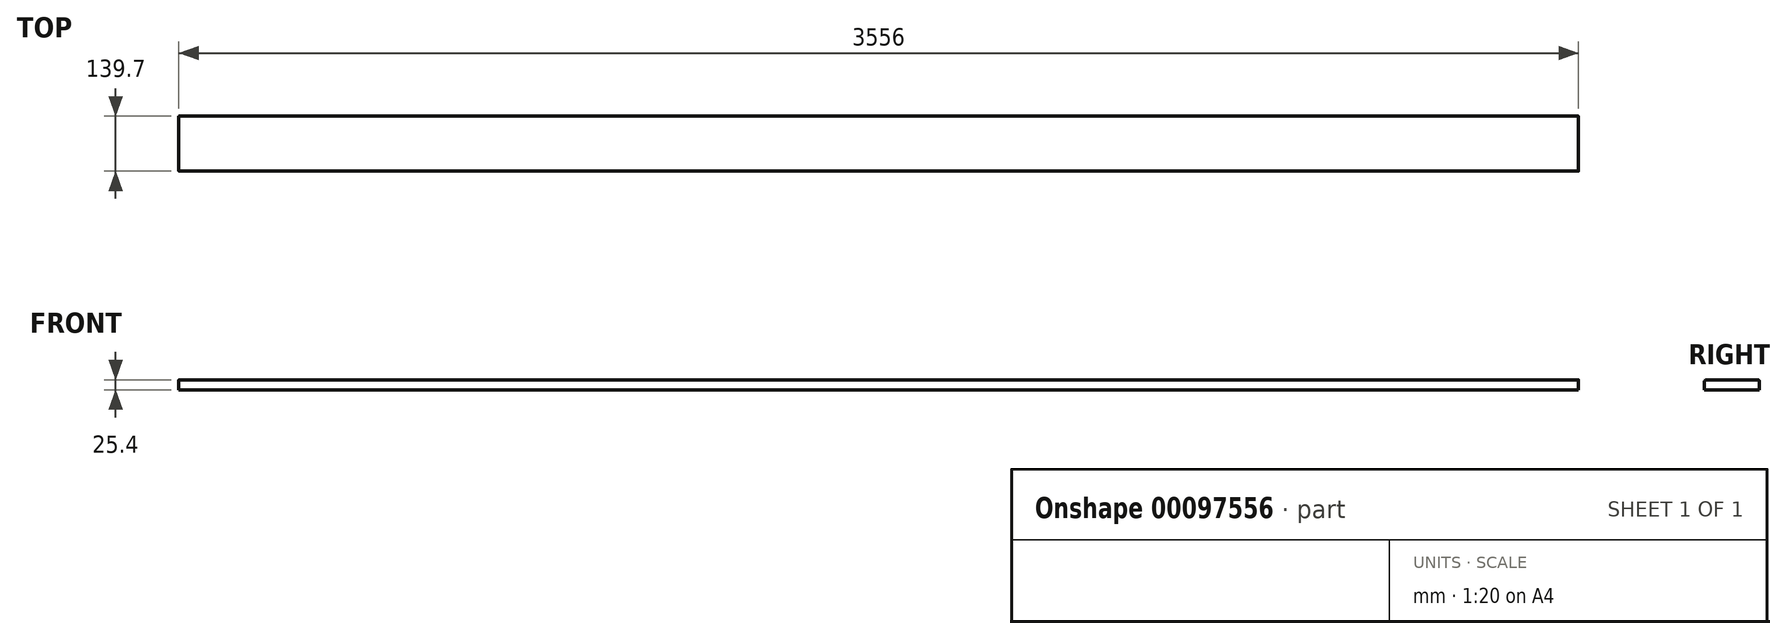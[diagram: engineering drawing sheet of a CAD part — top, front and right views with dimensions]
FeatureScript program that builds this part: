
annotation { "Feature Type Name" : "Feature", "Feature Type Description" : "" }
export const myFeature = defineFeature(function(context is Context, id is Id, definition is map)
    precondition{}
    {
        {
            var Q0;
            Q0=qCreatedBy(makeId("Top.planeOp"),FACE);
            var sketch = newSketch(context, id + "F0", { "sketchPlane" : qUnion([Q0])});
            skLineSegment(sketch, "E0.bottom", {"start": v(1778, 69.85) * mm, "end": v(-1778, 69.85) * mm});
            skLineSegment(sketch, "E0.top", {"start": v(1778, -69.85) * mm, "end": v(-1778, -69.85) * mm});
            skLineSegment(sketch, "E0.left", {"start": v(1778, 69.85) * mm, "end": v(1778, -69.85) * mm});
            skLineSegment(sketch, "E0.right", {"start": v(-1778, 69.85) * mm, "end": v(-1778, -69.85) * mm});
            skPoint(sketch, "E0.middle", {"position": v(0, 0) * mm});
            skSolve(sketch);
        }
        {
            var Q0;
            Q0=makeQuery(id+"F0.imprint","IMPRINT",FACE,{"disambiguationData":[TD([[makeQuery(id+"F0.imprint","IMPRINT",EDGE,{"derivedFrom":sQuery(id+"F0.wireOp",EDGE,"E0.bottom")}),1.0]])]});
            extrude(context, id + "F1", {"entities" : qUnion([Q0]), "depth" : 25.4 * mm});
        }
        {
            var Q0;
            Q0=makeQuery(id+"F1.opExtrude","CAP_EDGE",EDGE,{"disambiguationData":[OSD([sQuery(id+"F0.wireOp",EDGE,"E0.top")])],"isStart":false});
            fillet(context, id + "F2", {"entities" : qUnion([Q0]), "radius" : 5.08 * mm, "tangentPropagation" : true, "allowEdgeOverflow" : false});
        }
        {
            var Q0;
            Q0=makeQuery(id+"F1.opExtrude","CAP_EDGE",EDGE,{"disambiguationData":[OSD([sQuery(id+"F0.wireOp",EDGE,"E0.bottom")])],"isStart":false});
            fillet(context, id + "F3", {"entities" : qUnion([Q0]), "radius" : 5.08 * mm, "tangentPropagation" : true, "allowEdgeOverflow" : false});
        }
    });
